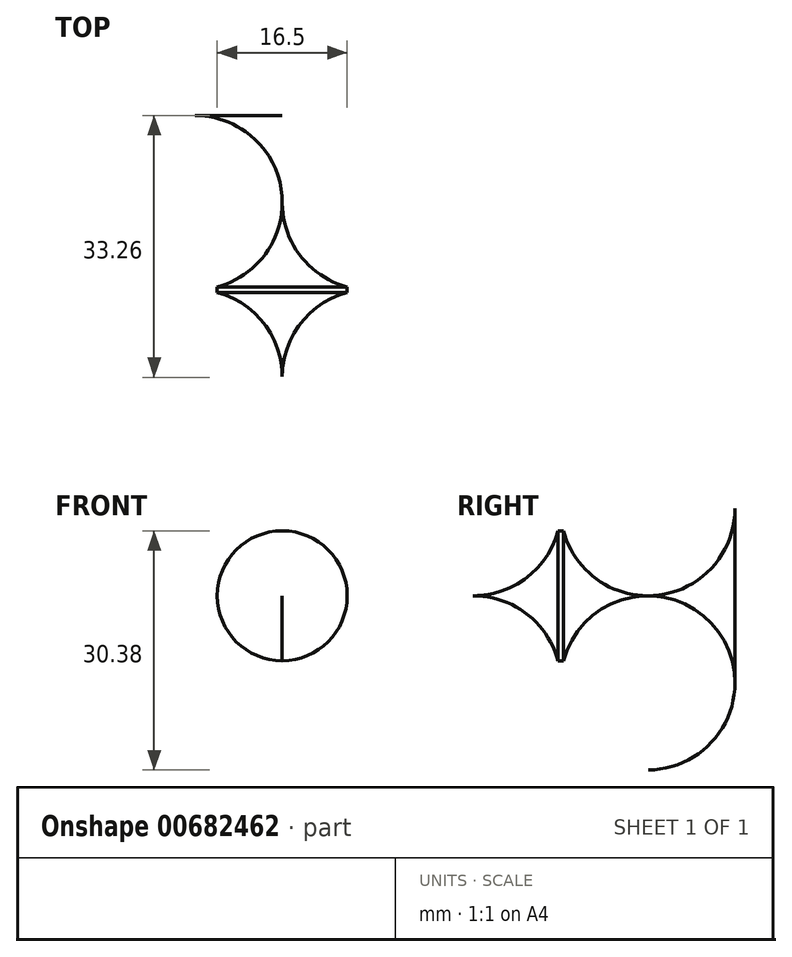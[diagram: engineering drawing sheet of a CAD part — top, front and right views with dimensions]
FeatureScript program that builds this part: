
annotation { "Feature Type Name" : "Feature", "Feature Type Description" : "" }
export const myFeature = defineFeature(function(context is Context, id is Id, definition is map)
    precondition{}
    {
        {
            var Q0;
            Q0=qCreatedBy(makeId("Top.planeOp"),FACE);
            var sketch = newSketch(context, id + "F0", { "sketchPlane" : qUnion([Q0])});
            skLineSegment(sketch, "E0", {"start": v(0, 0) * mm, "end": v(0, 22) * mm});
            skLineSegment(sketch, "E1", {"start": v(0, 11) * mm, "end": v(11.06, 11) * mm});
            skArc(sketch, "E2", {"start": v(0, 22) * mm, "mid": v(3.26, 14.22) * mm, "end": v(11.06, 11) * mm});
            skArc(sketch, "E3", {"start": v(11.06, 11) * mm, "mid": v(3.26, 7.78) * mm, "end": v(0, 0) * mm});
            skLineSegment(sketch, "E4", {"start": v(8.25, 11.36) * mm, "end": v(8.25, 10.64) * mm});
            skSolve(sketch);
        }
        {
            var Q0;
            {var subQ0=sQuery(id+"F0.wireOp",EDGE,"E2");var subQ1=sQuery(id+"F0.wireOp",EDGE,"E0");var subQ2=makeQuery(id+"F0.imprint","INTERSECT",VERTEX,{"derivedFrom":[subQ1,subQ0]});Q0=makeQuery(id+"F0.imprint","IMPRINT",FACE,{"disambiguationData":[TD([[makeQuery(id+"F0.imprint","IMPRINT",EDGE,{"disambiguationData":[TD([[subQ2,1.0]])],"derivedFrom":subQ1}),-1.0]])]});}
            var Q1;
            {var subQ0=sQuery(id+"F0.wireOp",EDGE,"E3");var subQ1=sQuery(id+"F0.wireOp",EDGE,"E0");var subQ2=makeQuery(id+"F0.imprint","INTERSECT",VERTEX,{"derivedFrom":[subQ1,subQ0]});Q1=makeQuery(id+"F0.imprint","IMPRINT",FACE,{"disambiguationData":[TD([[makeQuery(id+"F0.imprint","IMPRINT",EDGE,{"disambiguationData":[TD([[subQ2,-1.0]])],"derivedFrom":subQ1}),-1.0]])]});}
            var Q2;
            Q2=sQuery(id+"F0.wireOp",EDGE,"E0");
            revolve(context, id + "F1", {"entities" : qUnion([Q0, Q1]), "axis" : qUnion([Q2]), "revolveType" : RevolveType.FULL});
        }
    });
